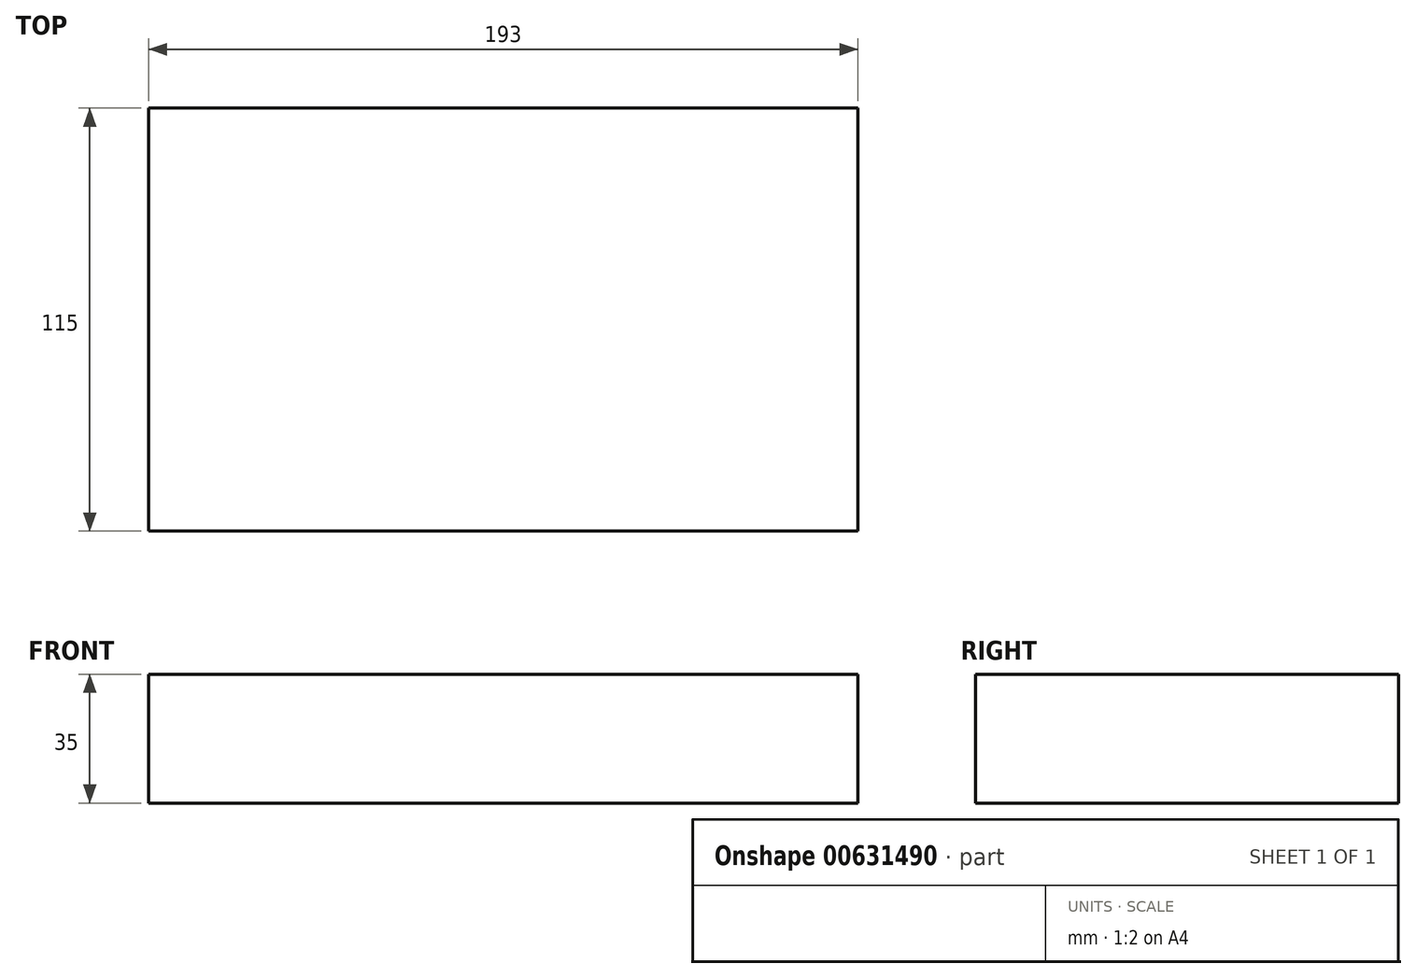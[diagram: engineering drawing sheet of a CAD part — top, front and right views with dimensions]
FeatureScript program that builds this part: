
annotation { "Feature Type Name" : "Feature", "Feature Type Description" : "" }
export const myFeature = defineFeature(function(context is Context, id is Id, definition is map)
    precondition{}
    {
        {
            assignVariable(context, id + "F0", {"name" : "hoehe", "anyValue" : 35 * mm});
        }
        {
            var Q0;
            Q0=qCreatedBy(makeId("Top.planeOp"),FACE);
            var sketch = newSketch(context, id + "F1", { "sketchPlane" : qUnion([Q0])});
            skLineSegment(sketch, "E0.bottom", {"start": v(-142.4, 77.24) * mm, "end": v(50.6, 77.24) * mm});
            skLineSegment(sketch, "E0.top", {"start": v(-142.4, -37.76) * mm, "end": v(50.6, -37.76) * mm});
            skLineSegment(sketch, "E0.left", {"start": v(-142.4, 77.24) * mm, "end": v(-142.4, -37.76) * mm});
            skLineSegment(sketch, "E0.right", {"start": v(50.6, 77.24) * mm, "end": v(50.6, -37.76) * mm});
            skSolve(sketch);
        }
        {
            var Q0;
            Q0=makeQuery(id+"F1.imprint","IMPRINT",FACE,{"disambiguationData":[TD([[makeQuery(id+"F1.imprint","IMPRINT",EDGE,{"derivedFrom":sQuery(id+"F1.wireOp",EDGE,"E0.bottom")}),-1.0]])]});
            extrude(context, id + "F2", {"entities" : qUnion([Q0]), "depth" : getVariable(context, 'hoehe'), "offsetDistance" : 25 * mm});
        }
    });
